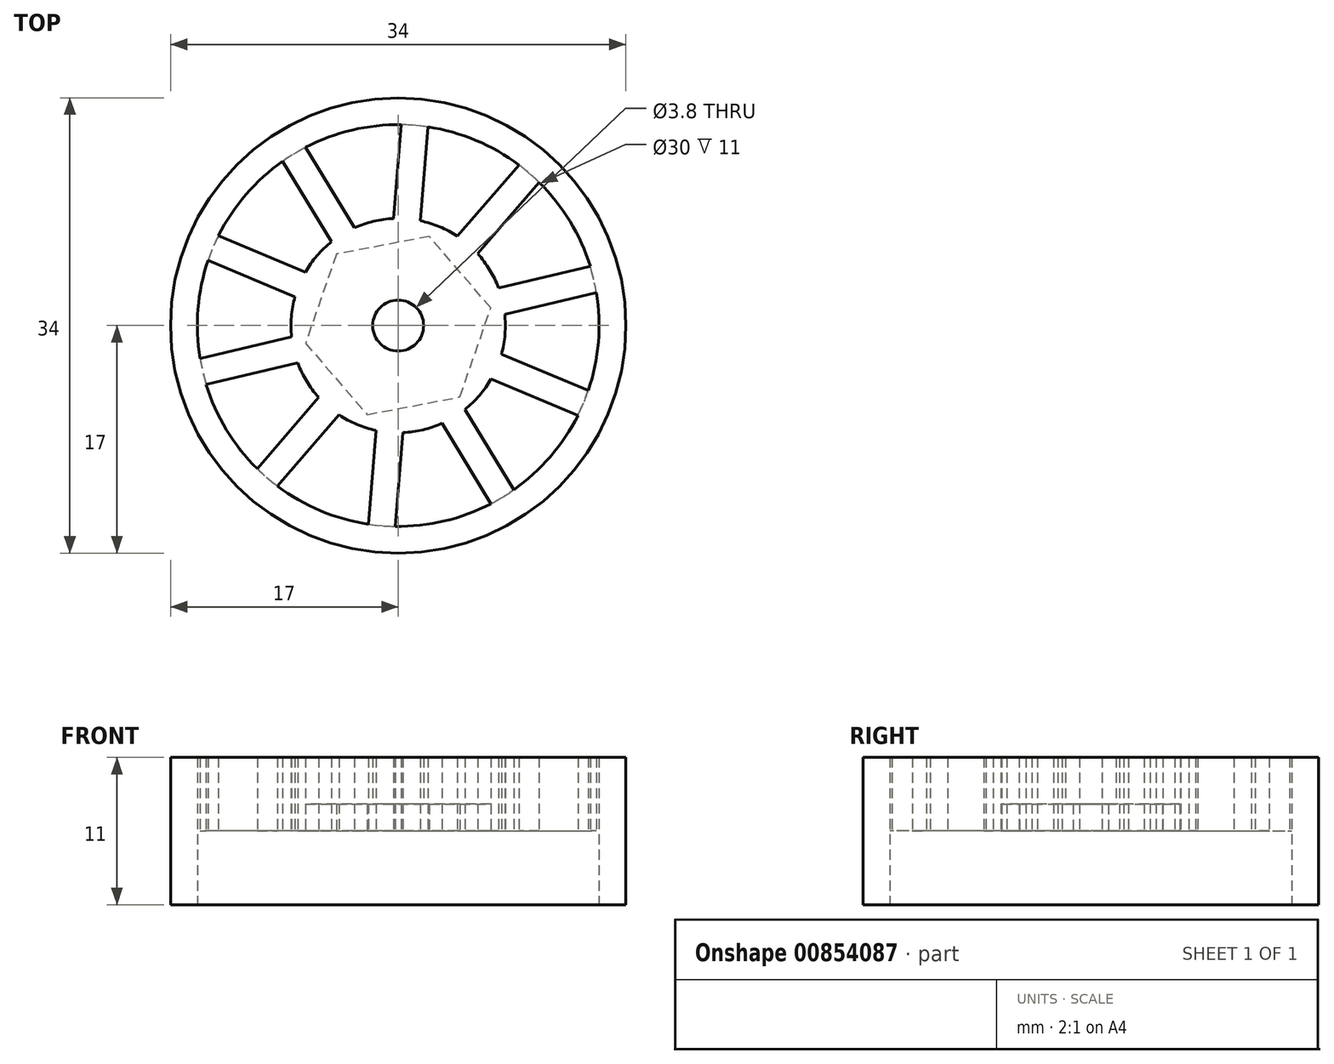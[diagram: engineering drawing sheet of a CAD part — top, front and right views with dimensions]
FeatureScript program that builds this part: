
annotation { "Feature Type Name" : "Feature", "Feature Type Description" : "" }
export const myFeature = defineFeature(function(context is Context, id is Id, definition is map)
    precondition{}
    {
        {
            var Q0;
            Q0=qCreatedBy(makeId("Top.planeOp"),FACE);
            var sketch = newSketch(context, id + "F0", { "sketchPlane" : qUnion([Q0])});
            skArc(sketch, "E0", {"start": v(-4.42, -6.67) * mm, "mid": v(-3.09, -7.38) * mm, "end": v(-1.65, -7.83) * mm});
            skArc(sketch, "E1", {"start": v(-14.34, -4.41) * mm, "mid": v(-12.82, -7.79) * mm, "end": v(-10.52, -10.7) * mm});
            skCircle(sketch, "E2", {"center": v(0, 0) * mm, "radius": 17 * mm});
            skLineSegment(sketch, "E3.0", {"start": v(-3.27, 7.3) * mm, "end": v(-6.92, 13.31) * mm});
            skLineSegment(sketch, "E4.0", {"start": v(-4.98, 6.26) * mm, "end": v(-8.63, 12.27) * mm});
            skLineSegment(sketch, "E5.1.0", {"start": v(-6.94, 3.99) * mm, "end": v(-13.42, 6.7) * mm});
            skLineSegment(sketch, "E5.1.1", {"start": v(-7.7, 2.14) * mm, "end": v(-14.2, 4.86) * mm});
            skLineSegment(sketch, "E5.2.0", {"start": v(-7.95, -0.85) * mm, "end": v(-14.8, -2.46) * mm});
            skLineSegment(sketch, "E5.2.1", {"start": v(-7.5, -2.8) * mm, "end": v(-14.34, -4.41) * mm});
            skLineSegment(sketch, "E5.3.0", {"start": v(-5.94, -5.36) * mm, "end": v(-10.52, -10.7) * mm});
            skLineSegment(sketch, "E5.3.1", {"start": v(-4.42, -6.67) * mm, "end": v(-9, -12) * mm});
            skLineSegment(sketch, "E5.4.0", {"start": v(-1.65, -7.83) * mm, "end": v(-2.23, -14.83) * mm});
            skLineSegment(sketch, "E5.4.1", {"start": v(0.34, -8) * mm, "end": v(-0.23, -15) * mm});
            skLineSegment(sketch, "E5.5.0", {"start": v(3.27, -7.3) * mm, "end": v(6.92, -13.31) * mm});
            skLineSegment(sketch, "E5.5.1", {"start": v(4.98, -6.26) * mm, "end": v(8.63, -12.27) * mm});
            skLineSegment(sketch, "E5.6.0", {"start": v(6.94, -3.99) * mm, "end": v(13.42, -6.7) * mm});
            skLineSegment(sketch, "E5.6.1", {"start": v(7.7, -2.14) * mm, "end": v(14.2, -4.86) * mm});
            skLineSegment(sketch, "E5.7.0", {"start": v(7.95, 0.85) * mm, "end": v(14.8, 2.46) * mm});
            skLineSegment(sketch, "E5.7.1", {"start": v(7.5, 2.8) * mm, "end": v(14.34, 4.41) * mm});
            skLineSegment(sketch, "E5.8.0", {"start": v(5.94, 5.36) * mm, "end": v(10.52, 10.7) * mm});
            skLineSegment(sketch, "E5.8.1", {"start": v(4.42, 6.67) * mm, "end": v(9, 12) * mm});
            skLineSegment(sketch, "E5.9.0", {"start": v(1.65, 7.83) * mm, "end": v(2.23, 14.83) * mm});
            skLineSegment(sketch, "E5.9.1", {"start": v(-0.34, 8) * mm, "end": v(0.23, 15) * mm});
            skArc(sketch, "E6.trimOffspring", {"start": v(-8.63, 12.27) * mm, "mid": v(-11.37, 9.79) * mm, "end": v(-13.42, 6.7) * mm});
            skArc(sketch, "E7.trimOffspring", {"start": v(-14.2, 4.86) * mm, "mid": v(-14.95, 1.23) * mm, "end": v(-14.8, -2.46) * mm});
            skArc(sketch, "E8.trimOffspring", {"start": v(0.23, 15) * mm, "mid": v(-3.45, 14.6) * mm, "end": v(-6.92, 13.31) * mm});
            skArc(sketch, "E9.trimOffspring", {"start": v(9, 12) * mm, "mid": v(5.8, 13.84) * mm, "end": v(2.23, 14.83) * mm});
            skArc(sketch, "E10.trimOffspring", {"start": v(14.34, 4.41) * mm, "mid": v(12.82, 7.79) * mm, "end": v(10.52, 10.7) * mm});
            skArc(sketch, "E11.trimOffspring", {"start": v(-0.23, -15) * mm, "mid": v(3.45, -14.6) * mm, "end": v(6.92, -13.31) * mm});
            skArc(sketch, "E12.trimOffspring", {"start": v(-9, -12) * mm, "mid": v(-5.8, -13.84) * mm, "end": v(-2.23, -14.83) * mm});
            skArc(sketch, "E13.trimOffspring", {"start": v(8.63, -12.27) * mm, "mid": v(11.37, -9.79) * mm, "end": v(13.42, -6.7) * mm});
            skArc(sketch, "E14.trimOffspring", {"start": v(14.2, -4.86) * mm, "mid": v(14.95, -1.23) * mm, "end": v(14.8, 2.46) * mm});
            skArc(sketch, "E15.trimOffspring", {"start": v(0.34, -8) * mm, "mid": v(1.84, -7.79) * mm, "end": v(3.27, -7.3) * mm});
            skArc(sketch, "E16.trimOffspring", {"start": v(4.98, -6.26) * mm, "mid": v(6.06, -5.22) * mm, "end": v(6.94, -3.99) * mm});
            skArc(sketch, "E17.trimOffspring", {"start": v(7.7, -2.14) * mm, "mid": v(7.97, -0.66) * mm, "end": v(7.95, 0.85) * mm});
            skArc(sketch, "E18.trimOffspring", {"start": v(7.5, 2.8) * mm, "mid": v(6.84, 4.15) * mm, "end": v(5.94, 5.36) * mm});
            skArc(sketch, "E19.trimOffspring", {"start": v(4.42, 6.67) * mm, "mid": v(3.09, 7.38) * mm, "end": v(1.65, 7.83) * mm});
            skArc(sketch, "E20.trimOffspring", {"start": v(-0.34, 8) * mm, "mid": v(-1.84, 7.79) * mm, "end": v(-3.27, 7.3) * mm});
            skArc(sketch, "E21.trimOffspring", {"start": v(-4.98, 6.26) * mm, "mid": v(-6.06, 5.22) * mm, "end": v(-6.94, 3.99) * mm});
            skArc(sketch, "E22.trimOffspring", {"start": v(-7.7, 2.14) * mm, "mid": v(-7.97, 0.66) * mm, "end": v(-7.95, -0.85) * mm});
            skCircle(sketch, "E23", {"center": v(0, 0) * mm, "radius": 1.9 * mm});
            skArc(sketch, "E24.trimOffspring", {"start": v(-7.5, -2.8) * mm, "mid": v(-6.84, -4.15) * mm, "end": v(-5.94, -5.36) * mm});
            skSolve(sketch);
        }
        {
            var Q0;
            Q0 = qSketchRegion(id + "F0", true);
            extrude(context, id + "F1", {"entities" : qUnion([Q0]), "depth" : 11 * mm, "offsetDistance" : 25 * mm});
        }
        {
            var Q0;
            Q0=qCreatedBy(makeId("Top.planeOp"),FACE);
            var sketch = newSketch(context, id + "F2", { "sketchPlane" : qUnion([Q0])});
            skCircle(sketch, "E25", {"center": v(0, 0) * mm, "radius": 15 * mm});
            skSolve(sketch);
        }
        {
            var Q0;
            Q0 = qSketchRegion(id + "F2", true);
            extrude(context, id + "F3", {"entities" : qUnion([Q0]), "operationType" : NewBodyOperationType.REMOVE, "depth" : 5.5 * mm, "offsetDistance" : 25 * mm});
        }
        {
            var Q0;
            Q0=qCreatedBy(makeId("Top.planeOp"),FACE);
            cPlane(context, id + "F4", {"entities" : qUnion([Q0]), "cplaneType" : CPlaneType.OFFSET, "offset" : 5 * mm, "width" : 150 * mm, "height" : 150 * mm});
        }
        {
            var Q0;
            Q0=qCreatedBy(id+"F4.planeOp",FACE);
            var sketch = newSketch(context, id + "F5", { "sketchPlane" : qUnion([Q0])});
            skCircle(sketch, "E26.cCircle", {"center": v(0, 0) * mm, "radius": 6.1 * mm, "construction": true});
            skLineSegment(sketch, "E26.0", {"start": v(4.6, -5.34) * mm, "end": v(-2.32, -6.65) * mm});
            skLineSegment(sketch, "E26.1", {"start": v(-2.32, -6.65) * mm, "end": v(-6.92, -1.32) * mm});
            skLineSegment(sketch, "E26.2", {"start": v(-6.92, -1.32) * mm, "end": v(-4.6, 5.34) * mm});
            skLineSegment(sketch, "E26.3", {"start": v(-4.6, 5.34) * mm, "end": v(2.32, 6.65) * mm});
            skLineSegment(sketch, "E26.4", {"start": v(2.32, 6.65) * mm, "end": v(6.92, 1.32) * mm});
            skLineSegment(sketch, "E26.5", {"start": v(6.92, 1.32) * mm, "end": v(4.6, -5.34) * mm});
            skPoint(sketch, "E26.0.midPoint", {"position": v(1.14, -6) * mm});
            skSolve(sketch);
        }
        {
            var Q0;
            Q0 = qSketchRegion(id + "F5", true);
            extrude(context, id + "F6", {"entities" : qUnion([Q0]), "operationType" : NewBodyOperationType.REMOVE, "depth" : 2.5 * mm, "offsetDistance" : 25 * mm});
        }
    });
